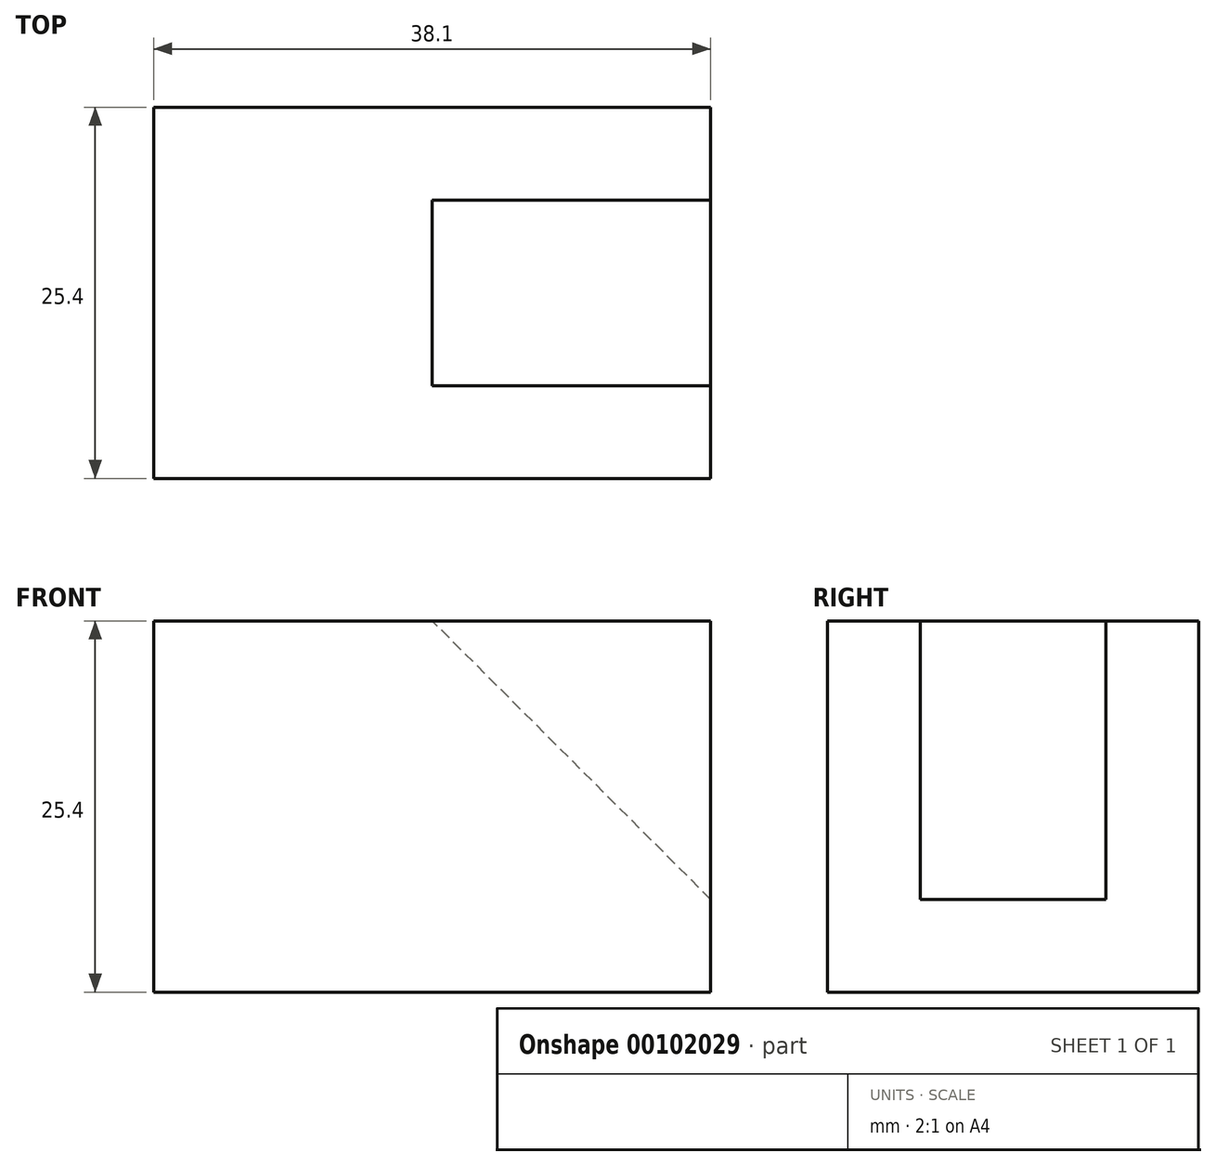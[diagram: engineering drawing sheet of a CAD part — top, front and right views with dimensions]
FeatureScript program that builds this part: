
annotation { "Feature Type Name" : "Feature", "Feature Type Description" : "" }
export const myFeature = defineFeature(function(context is Context, id is Id, definition is map)
    precondition{}
    {
        {
            var Q0;
            Q0=qCreatedBy(makeId("Front.planeOp"),FACE);
            var sketch = newSketch(context, id + "F0", { "sketchPlane" : qUnion([Q0])});
            skLineSegment(sketch, "E0", {"start": v(0, 0) * mm, "end": v(38.1, 0) * mm});
            skLineSegment(sketch, "E1", {"start": v(38.1, 0) * mm, "end": v(38.1, 25.4) * mm});
            skLineSegment(sketch, "E2", {"start": v(38.1, 25.4) * mm, "end": v(0, 25.4) * mm});
            skLineSegment(sketch, "E3", {"start": v(0, 25.4) * mm, "end": v(0, 0) * mm});
            skSolve(sketch);
        }
        {
            var Q0;
            Q0=qCreatedBy(makeId("Front.planeOp"),FACE);
            var sketch = newSketch(context, id + "F1", { "sketchPlane" : qUnion([Q0])});
            skLineSegment(sketch, "E4", {"start": v(38.1, 25.4) * mm, "end": v(38.1, 6.35) * mm});
            skLineSegment(sketch, "E5", {"start": v(38.1, 6.35) * mm, "end": v(19.05, 25.4) * mm});
            skLineSegment(sketch, "E6", {"start": v(19.05, 25.4) * mm, "end": v(38.1, 25.4) * mm});
            skSolve(sketch);
        }
        {
            var Q0;
            Q0 = qSketchRegion(id + "F0", true);
            extrude(context, id + "F2", {"entities" : qUnion([Q0]), "oppositeDirection" : true, "depth" : 25.4 * mm});
        }
        {
            var Q0;
            Q0 = qSketchRegion(id + "F1", true);
            extrude(context, id + "F3", {"entities" : qUnion([Q0]), "operationType" : NewBodyOperationType.REMOVE, "oppositeDirection" : true, "depth" : 19.05 * mm, "hasSecondDirection" : true, "secondDirectionOppositeDirection" : true, "secondDirectionDepth" : 6.35 * mm});
        }
    });
